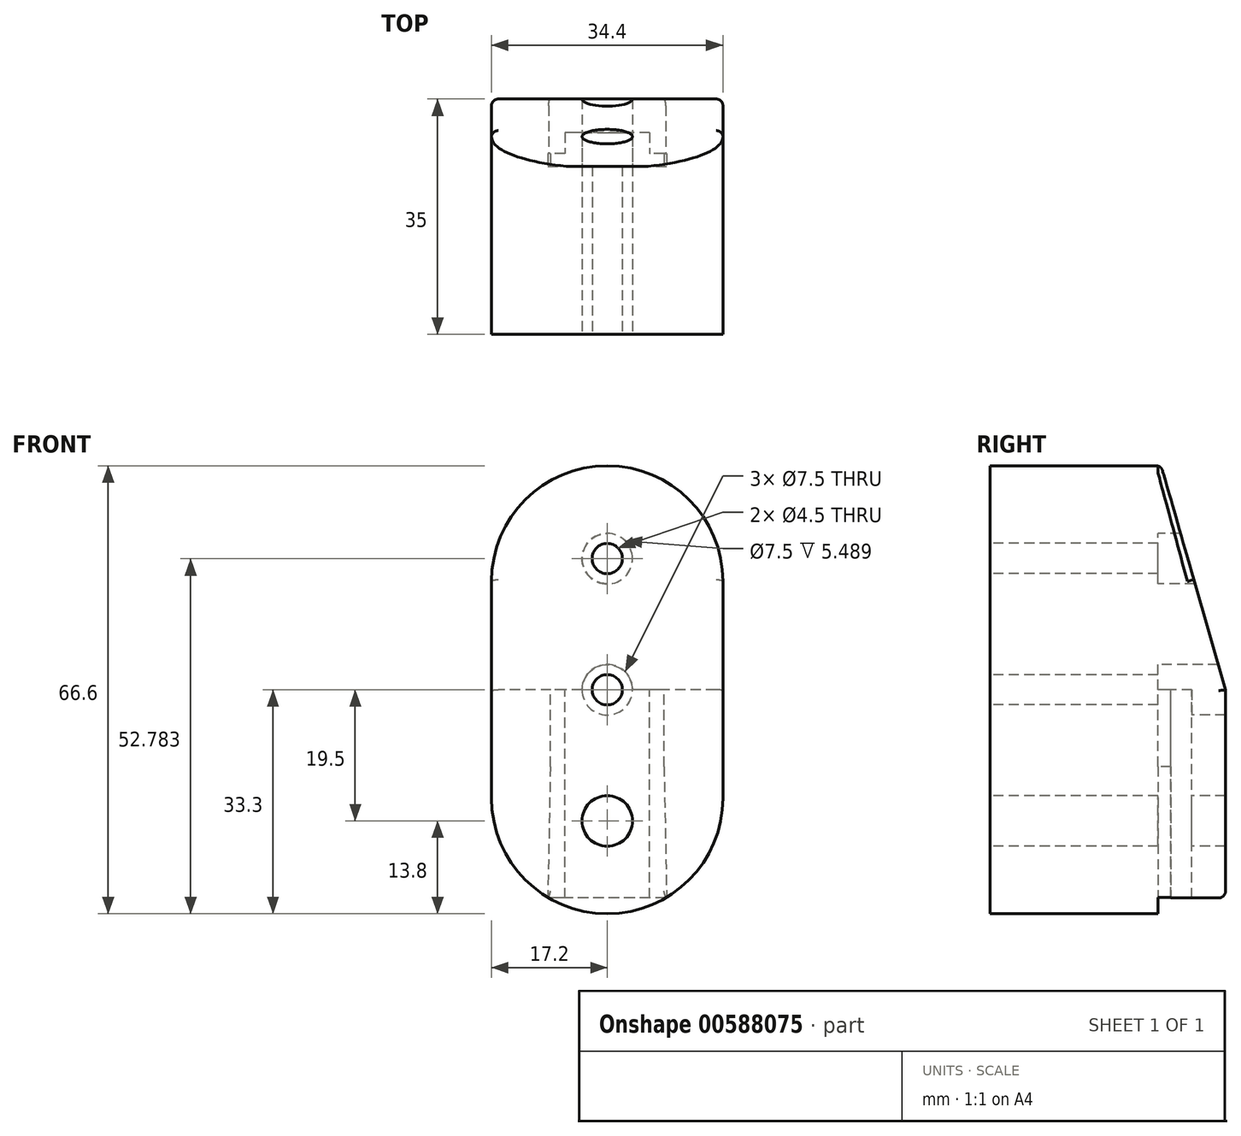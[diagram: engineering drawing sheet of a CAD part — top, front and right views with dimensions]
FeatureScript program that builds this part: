
annotation { "Feature Type Name" : "Feature", "Feature Type Description" : "" }
export const myFeature = defineFeature(function(context is Context, id is Id, definition is map)
    precondition{}
    {
        {
            var Q0;
            Q0=qCreatedBy(makeId("Front.planeOp"),FACE);
            var sketch = newSketch(context, id + "F0", { "sketchPlane" : qUnion([Q0])});
            skLineSegment(sketch, "E0", {"start": v(0, 0) * mm, "end": v(0, 2.25) * mm, "construction": true});
            skLineSegment(sketch, "E1", {"start": v(0, 0) * mm, "end": v(0, -2.25) * mm, "construction": true});
            skArc(sketch, "E2", {"start": v(-17.2, -16.1) * mm, "mid": v(0, -33.3) * mm, "end": v(17.2, -16.1) * mm});
            skLineSegment(sketch, "E3", {"start": v(17.2, 16.1) * mm, "end": v(17.2, -16.1) * mm});
            skLineSegment(sketch, "E4", {"start": v(-17.2, 16.1) * mm, "end": v(-17.2, -16.1) * mm});
            skArc(sketch, "E5.trimOffspring", {"start": v(17.2, 16.1) * mm, "mid": v(0, 33.3) * mm, "end": v(-17.2, 16.1) * mm});
            skCircle(sketch, "E6", {"center": v(0, 0) * mm, "radius": 2.25 * mm});
            skCircle(sketch, "E7", {"center": v(0, 19.5) * mm, "radius": 2.25 * mm});
            skCircle(sketch, "E8", {"center": v(0, -19.5) * mm, "radius": 2.25 * mm});
            skLineSegment(sketch, "E9.trimOffspring", {"start": v(0, 16.1) * mm, "end": v(0, 19.5) * mm, "construction": true});
            skLineSegment(sketch, "E10.trimOffspring", {"start": v(0, -16.1) * mm, "end": v(0, -19.5) * mm, "construction": true});
            skLineSegment(sketch, "E11", {"start": v(0, -33.3) * mm, "end": v(0, -10.8) * mm, "construction": true});
            skLineSegment(sketch, "E12", {"start": v(0, -10.8) * mm, "end": v(-8.25, -10.8) * mm, "construction": true});
            skLineSegment(sketch, "E13", {"start": v(0, -10.8) * mm, "end": v(8.25, -10.8) * mm, "construction": true});
            skCircle(sketch, "E14", {"center": v(0, -19.5) * mm, "radius": 3.75 * mm});
            skSolve(sketch);
        }
        {
            var Q0;
            Q0 = qSketchRegion(id + "F0", true);
            extrude(context, id + "F1", {"entities" : qUnion([Q0]), "oppositeDirection" : true, "depth" : 10 * mm, "offsetDistance" : 25 * mm, "hasSecondDirection" : true, "secondDirectionOppositeDirection" : false, "secondDirectionDepth" : 5 * mm});
        }
        {
            var Q0;
            Q0=qCreatedBy(makeId("Front.planeOp"),FACE);
            var sketch = newSketch(context, id + "F2", { "sketchPlane" : qUnion([Q0])});
            skLineSegment(sketch, "E15", {"start": v(0, -33.3) * mm, "end": v(8.88, -33.3) * mm});
            skLineSegment(sketch, "E16", {"start": v(0, -33.3) * mm, "end": v(-8.88, -33.3) * mm});
            skLineSegment(sketch, "E17", {"start": v(0, -33.3) * mm, "end": v(0, -11.4) * mm, "construction": true});
            skLineSegment(sketch, "E18", {"start": v(0, -11.4) * mm, "end": v(-8.45, -11.4) * mm, "construction": true});
            skLineSegment(sketch, "E19", {"start": v(0, -11.4) * mm, "end": v(8.45, -11.4) * mm, "construction": true});
            skLineSegment(sketch, "E20", {"start": v(8.45, -11.4) * mm, "end": v(8.88, -33.3) * mm});
            skLineSegment(sketch, "E21", {"start": v(-8.45, -11.4) * mm, "end": v(-8.88, -33.3) * mm});
            skPoint(sketch, "E22.end.orphan", {"position": v(0, 0) * mm});
            skPoint(sketch, "E23.MirrorCS.start.orphan", {"position": v(6.3, 0) * mm});
            skPoint(sketch, "E24.MirrorCS.start.orphan", {"position": v(6.3, -33.3) * mm});
            skPoint(sketch, "E25.orphan", {"position": v(-6.3, -33.3) * mm});
            skPoint(sketch, "E26.end.orphan", {"position": v(-6.3, 0) * mm});
            skLineSegment(sketch, "E27", {"start": v(-8.45, -11.4) * mm, "end": v(-8.45, 0) * mm});
            skLineSegment(sketch, "E28", {"start": v(-8.45, 0) * mm, "end": v(0, 0) * mm});
            skLineSegment(sketch, "E29.MirrorCS", {"start": v(8.45, -11.4) * mm, "end": v(8.45, 0) * mm});
            skLineSegment(sketch, "E30.MirrorCS", {"start": v(8.45, 0) * mm, "end": v(0, 0) * mm});
            skSolve(sketch);
        }
        {
            var Q0;
            Q0=qCreatedBy(makeId("Front.planeOp"),FACE);
            var sketch = newSketch(context, id + "F3", { "sketchPlane" : qUnion([Q0])});
            skLineSegment(sketch, "E31", {"start": v(0, -34.55) * mm, "end": v(-6.3, -34.55) * mm});
            skLineSegment(sketch, "E32", {"start": v(-6.3, -34.55) * mm, "end": v(-6.3, 0) * mm});
            skLineSegment(sketch, "E33", {"start": v(-6.3, 0) * mm, "end": v(0, 0) * mm});
            skLineSegment(sketch, "E34.MirrorCS", {"start": v(6.3, -34.55) * mm, "end": v(6.3, 0) * mm});
            skLineSegment(sketch, "E35.MirrorCS", {"start": v(6.3, 0) * mm, "end": v(0, 0) * mm});
            skLineSegment(sketch, "E36.MirrorCS", {"start": v(0, -34.55) * mm, "end": v(6.3, -34.55) * mm});
            skSolve(sketch);
        }
        {
            var Q0;
            Q0 = qSketchRegion(id + "F2", true);
            extrude(context, id + "F4", {"entities" : qUnion([Q0]), "operationType" : NewBodyOperationType.REMOVE, "oppositeDirection" : true, "depth" : 1.9 * mm, "offsetDistance" : 25 * mm});
        }
        {
            var Q0;
            Q0=makeQuery(id+"F3.imprint","IMPRINT",FACE,{"disambiguationData":[TD([[makeQuery(id+"F3.imprint","IMPRINT",EDGE,{"derivedFrom":sQuery(id+"F3.wireOp",EDGE,"E31")}),-1.0]])]});
            extrude(context, id + "F5", {"entities" : qUnion([Q0]), "operationType" : NewBodyOperationType.REMOVE, "oppositeDirection" : true, "depth" : 5 * mm, "offsetDistance" : 25 * mm});
        }
        {
            var Q0;
            Q0=qCreatedBy(makeId("Right.planeOp"),FACE);
            var sketch = newSketch(context, id + "F6", { "sketchPlane" : qUnion([Q0])});
            skLineSegment(sketch, "E37", {"start": v(10, 0) * mm, "end": v(10, 64.58) * mm});
            skLineSegment(sketch, "E38", {"start": v(10, 64.58) * mm, "end": v(-8.52, 64.58) * mm});
            skLineSegment(sketch, "E39", {"start": v(-8.52, 64.58) * mm, "end": v(10, 0) * mm});
            skSolve(sketch);
        }
        {
            var Q0;
            Q0=makeQuery(id+"F6.imprint","IMPRINT",FACE,{"disambiguationData":[TD([[makeQuery(id+"F6.imprint","IMPRINT",EDGE,{"derivedFrom":sQuery(id+"F6.wireOp",EDGE,"E37")}),1.0]])]});
            extrude(context, id + "F7", {"entities" : qUnion([Q0]), "operationType" : NewBodyOperationType.REMOVE, "endBound" : BoundingType.SYMMETRIC, "depth" : 40 * mm, "offsetDistance" : 25 * mm});
        }
        {
            var Q0;
            Q0=qCreatedBy(makeId("Right.planeOp"),FACE);
            var sketch = newSketch(context, id + "F8", { "sketchPlane" : qUnion([Q0])});
            skLineSegment(sketch, "E40", {"start": v(-10.19, -30.94) * mm, "end": v(22.23, -30.94) * mm});
            skLineSegment(sketch, "E41", {"start": v(22.23, -30.94) * mm, "end": v(22.23, -41.9) * mm});
            skLineSegment(sketch, "E42", {"start": v(22.23, -41.9) * mm, "end": v(-10.19, -41.9) * mm});
            skLineSegment(sketch, "E43", {"start": v(-10.19, -41.9) * mm, "end": v(-10.19, -30.94) * mm});
            skSolve(sketch);
        }
        {
            var Q0;
            Q0=makeQuery(id+"F8.imprint","IMPRINT",FACE,{"disambiguationData":[TD([[makeQuery(id+"F8.imprint","IMPRINT",EDGE,{"derivedFrom":sQuery(id+"F8.wireOp",EDGE,"E40")}),-1.0]])]});
            extrude(context, id + "F9", {"entities" : qUnion([Q0]), "operationType" : NewBodyOperationType.REMOVE, "endBound" : BoundingType.SYMMETRIC, "depth" : 40 * mm, "offsetDistance" : 25 * mm});
        }
        {
            var Q0;
            Q0=qCreatedBy(makeId("Front.planeOp"),FACE);
            var sketch = newSketch(context, id + "F10", { "sketchPlane" : qUnion([Q0])});
            skCircle(sketch, "E44", {"center": v(0, 0) * mm, "radius": 3.75 * mm});
            skCircle(sketch, "E45", {"center": v(0, 19.48) * mm, "radius": 3.75 * mm});
            skSolve(sketch);
        }
        {
            var Q0;
            Q0 = qSketchRegion(id + "F10", true);
            extrude(context, id + "F11", {"entities" : qUnion([Q0]), "operationType" : NewBodyOperationType.REMOVE, "oppositeDirection" : true, "depth" : 16.2 * mm, "offsetDistance" : 25 * mm});
        }
        {
            var Q0;
            Q0=makeQuery(id+"F11.boolean.opBoolean","INTERSECT",EDGE,{"derivedFrom":[makeQuery(id+"F1.opExtrude","SWEPT_FACE",FACE,{"disambiguationData":[OSD([sQuery(id+"F0.wireOp",EDGE,"E7")])]}),makeQuery(id+"F11.opExtrude","CAP_FACE",FACE,{"disambiguationData":[OSD([sQuery(id+"F10.wireOp",EDGE,"E45")])],"isStart":true})]});
            chamfer(context, id + "F12", {"entities" : qUnion([Q0]), "width" : 2.5 * mm, "tangentPropagation" : true});
        }
        {
            var Q0;
            Q0=makeQuery(id+"F11.boolean.opBoolean","INTERSECT",EDGE,{"derivedFrom":[makeQuery(id+"F1.opExtrude","SWEPT_FACE",FACE,{"disambiguationData":[OSD([sQuery(id+"F0.wireOp",EDGE,"E6")])]}),makeQuery(id+"F11.opExtrude","CAP_FACE",FACE,{"disambiguationData":[OSD([sQuery(id+"F10.wireOp",EDGE,"E44")])],"isStart":true})]});
            chamfer(context, id + "F13", {"entities" : qUnion([Q0]), "width" : 2.5 * mm, "tangentPropagation" : true});
        }
        {
            var Q0;
            Q0=makeQuery(id+"F7.boolean.opBoolean","INTERSECT",EDGE,{"derivedFrom":[makeQuery(id+"F1.opExtrude","SWEPT_FACE",FACE,{"disambiguationData":[OSD([sQuery(id+"F0.wireOp",EDGE,"E4")])]}),makeQuery(id+"F7.opExtrude","SWEPT_FACE",FACE,{"disambiguationData":[OSD([sQuery(id+"F6.wireOp",EDGE,"E39")])]})]});
            var Q1;
            Q1=makeQuery(id+"F7.boolean.opBoolean","INTERSECT",EDGE,{"derivedFrom":[makeQuery(id+"F1.opExtrude","SWEPT_FACE",FACE,{"disambiguationData":[OSD([sQuery(id+"F0.wireOp",EDGE,"E5.trimOffspring")])]}),makeQuery(id+"F7.opExtrude","SWEPT_FACE",FACE,{"disambiguationData":[OSD([sQuery(id+"F6.wireOp",EDGE,"E39")])]})]});
            var Q2;
            Q2=makeQuery(id+"F7.boolean.opBoolean","INTERSECT",EDGE,{"derivedFrom":[makeQuery(id+"F1.opExtrude","SWEPT_FACE",FACE,{"disambiguationData":[OSD([sQuery(id+"F0.wireOp",EDGE,"E3")])]}),makeQuery(id+"F7.opExtrude","SWEPT_FACE",FACE,{"disambiguationData":[OSD([sQuery(id+"F6.wireOp",EDGE,"E39")])]})]});
            var Q3;
            Q3=makeQuery(id+"F1.opExtrude","CAP_EDGE",EDGE,{"disambiguationData":[OSD([sQuery(id+"F0.wireOp",EDGE,"E3")])],"isStart":false});
            var Q4;
            {var subQ0=sQuery(id+"F0.wireOp",EDGE,"E2");var subQ1=sQuery(id+"F0.wireOp",EDGE,"E3");Q4=makeQuery(id+"F9.boolean.opBoolean","SPLIT",EDGE,{"disambiguationData":[TD([makeQuery(id+"F1.opExtrude","SWEPT_FACE",FACE,{"disambiguationData":[OSD([subQ1])]})])],"derivedFrom":makeQuery(id+"F1.opExtrude","CAP_EDGE",EDGE,{"disambiguationData":[OSD([subQ0])],"isStart":false})});}
            var Q5;
            {var subQ0=sQuery(id+"F0.wireOp",EDGE,"E2");var subQ1=sQuery(id+"F0.wireOp",EDGE,"E4");Q5=makeQuery(id+"F9.boolean.opBoolean","SPLIT",EDGE,{"disambiguationData":[TD([makeQuery(id+"F1.opExtrude","SWEPT_FACE",FACE,{"disambiguationData":[OSD([subQ1])]})])],"derivedFrom":makeQuery(id+"F1.opExtrude","CAP_EDGE",EDGE,{"disambiguationData":[OSD([subQ0])],"isStart":false})});}
            var Q6;
            Q6=makeQuery(id+"F1.opExtrude","CAP_EDGE",EDGE,{"disambiguationData":[OSD([sQuery(id+"F0.wireOp",EDGE,"E4")])],"isStart":false});
            var Q7;
            Q7=makeQuery(id+"F9.boolean.opBoolean","INTERSECT",EDGE,{"derivedFrom":[makeQuery(id+"F1.opExtrude","CAP_FACE",FACE,{"disambiguationData":[OSD([sQuery(id+"F0.wireOp",EDGE,"E2"),sQuery(id+"F0.wireOp",EDGE,"E3"),sQuery(id+"F0.wireOp",EDGE,"E4"),sQuery(id+"F0.wireOp",EDGE,"E5.trimOffspring"),sQuery(id+"F0.wireOp",EDGE,"E6"),sQuery(id+"F0.wireOp",EDGE,"E7"),sQuery(id+"F0.wireOp",EDGE,"E8")])],"isStart":false}),makeQuery(id+"F9.opExtrude","SWEPT_FACE",FACE,{"disambiguationData":[OSD([sQuery(id+"F8.wireOp",EDGE,"E40")])]})]});
            fillet(context, id + "F14", {"entities" : qUnion([Q0, Q1, Q2, Q3, Q4, Q5, Q6, Q7]), "radius" : 1 * mm, "tangentPropagation" : true, "allowEdgeOverflow" : false});
        }
        {
            var Q0;
            Q0=qCreatedBy(makeId("Front.planeOp"),FACE);
            var sketch = newSketch(context, id + "F15", { "sketchPlane" : qUnion([Q0])});
            skSolve(sketch);
        }
        {
            var Q0;
            Q0 = qSketchRegion(id + "F0", true);
            var Q1;
            Q1 = qSketchRegion(id + "F15", true);
            extrude(context, id + "F16", {"entities" : qUnion([Q0, Q1]), "operationType" : NewBodyOperationType.ADD, "depth" : 25 * mm, "offsetDistance" : 25 * mm});
        }
        {
            var Q0;
            Q0=makeQuery(id+"F0.imprint","IMPRINT",FACE,{"disambiguationData":[TD([[makeQuery(id+"F0.imprint","IMPRINT",EDGE,{"derivedFrom":sQuery(id+"F0.wireOp",EDGE,"E8")}),-1.0]])]});
            extrude(context, id + "F17", {"entities" : qUnion([Q0]), "operationType" : NewBodyOperationType.REMOVE, "depth" : 22 * mm, "offsetDistance" : 25 * mm});
        }
    });
